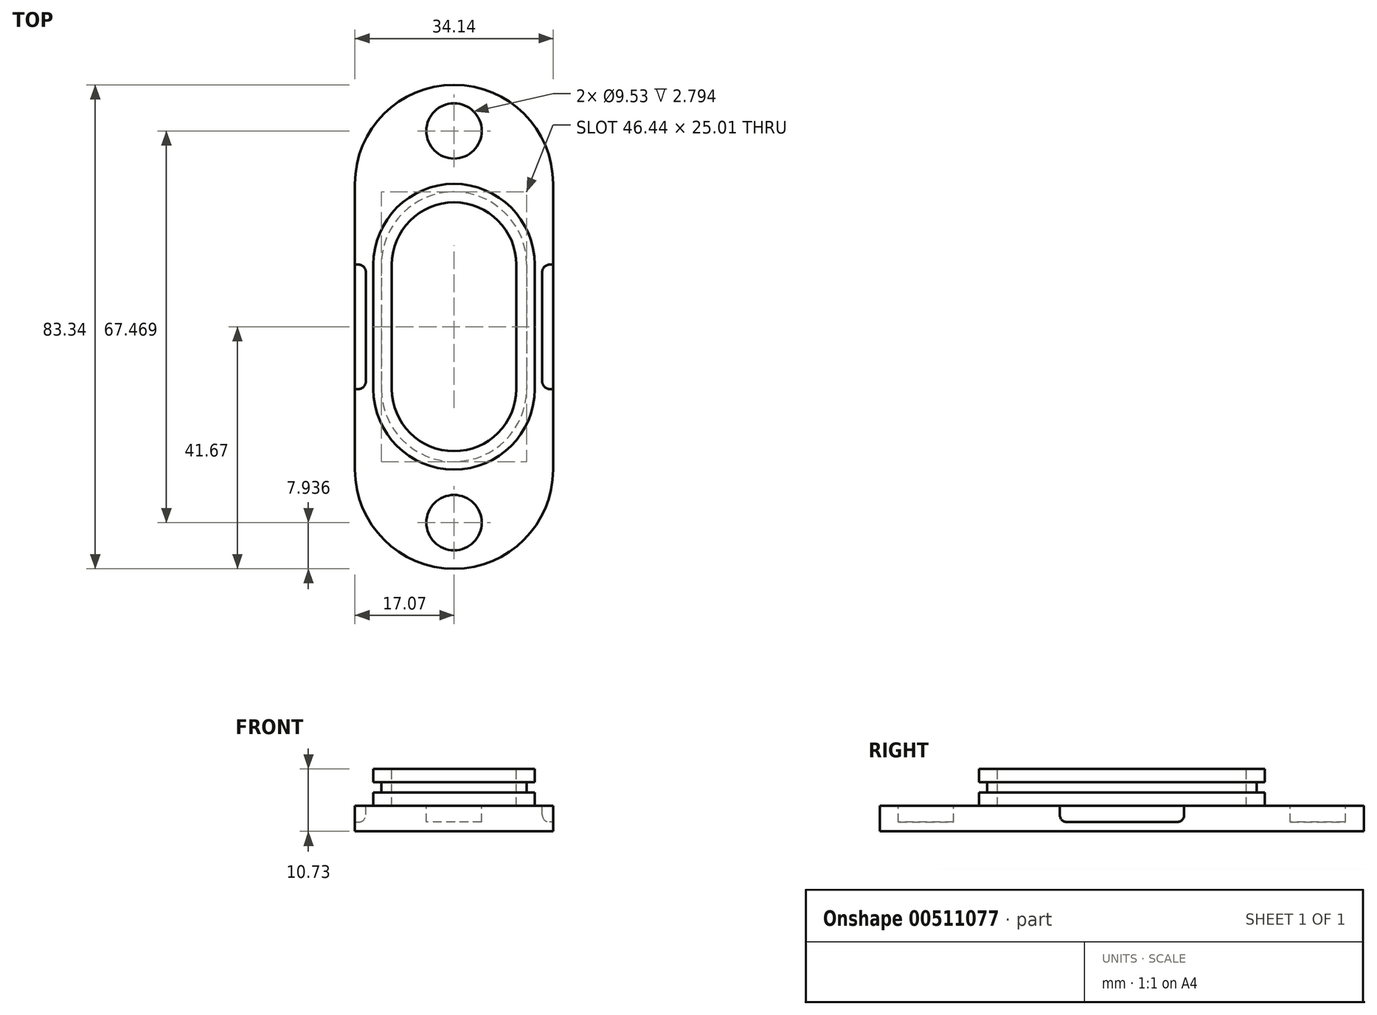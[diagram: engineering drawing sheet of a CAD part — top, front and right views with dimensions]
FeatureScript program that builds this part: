
annotation { "Feature Type Name" : "Feature", "Feature Type Description" : "" }
export const myFeature = defineFeature(function(context is Context, id is Id, definition is map)
    precondition{}
    {
        {
            var Q0;
            Q0=qCreatedBy(makeId("Top.planeOp"),FACE);
            var sketch = newSketch(context, id + "F0", { "sketchPlane" : qUnion([Q0])});
            skLineSegment(sketch, "E0.bottom", {"start": v(-13.9, 10.72) * mm, "end": v(13.9, 10.72) * mm, "construction": true});
            skLineSegment(sketch, "E0.top", {"start": v(-13.9, -10.72) * mm, "end": v(13.9, -10.72) * mm, "construction": true});
            skLineSegment(sketch, "E0.left", {"start": v(-13.9, 10.72) * mm, "end": v(-13.9, -10.72) * mm});
            skLineSegment(sketch, "E0.right", {"start": v(13.9, 10.72) * mm, "end": v(13.9, -10.72) * mm});
            skPoint(sketch, "E0.middle", {"position": v(0, 0) * mm});
            skArc(sketch, "E1", {"start": v(13.9, 10.72) * mm, "mid": v(0, 24.6) * mm, "end": v(-13.9, 10.72) * mm});
            skArc(sketch, "E2", {"start": v(-13.9, -10.72) * mm, "mid": v(0, -24.6) * mm, "end": v(13.9, -10.72) * mm});
            skLineSegment(sketch, "E3.bottom", {"start": v(-17.07, 24.6) * mm, "end": v(17.07, 24.6) * mm, "construction": true});
            skLineSegment(sketch, "E3.top", {"start": v(-17.07, -24.6) * mm, "end": v(17.07, -24.6) * mm, "construction": true});
            skLineSegment(sketch, "E3.left", {"start": v(-17.07, 24.6) * mm, "end": v(-17.07, -24.6) * mm});
            skLineSegment(sketch, "E3.right", {"start": v(17.07, 24.6) * mm, "end": v(17.07, -24.6) * mm});
            skArc(sketch, "E4", {"start": v(17.07, 24.6) * mm, "mid": v(0, 41.67) * mm, "end": v(-17.07, 24.6) * mm});
            skArc(sketch, "E5", {"start": v(-17.07, -24.6) * mm, "mid": v(0, -41.67) * mm, "end": v(17.07, -24.6) * mm});
            skCircle(sketch, "E6", {"center": v(0, 33.73) * mm, "radius": 4.76 * mm});
            skCircle(sketch, "E7", {"center": v(0, -33.73) * mm, "radius": 4.76 * mm});
            skArc(sketch, "E8.0", {"start": v(14.68, 10.72) * mm, "mid": v(0, 25.4) * mm, "end": v(-14.68, 10.72) * mm});
            skLineSegment(sketch, "E8.1", {"start": v(14.68, 10.72) * mm, "end": v(14.68, -10.72) * mm});
            skArc(sketch, "E8.2", {"start": v(-14.68, -10.72) * mm, "mid": v(0, -25.4) * mm, "end": v(14.68, -10.72) * mm});
            skLineSegment(sketch, "E8.3", {"start": v(-14.68, 10.72) * mm, "end": v(-14.68, -10.72) * mm});
            skSolve(sketch);
        }
        {
            var Q0;
            Q0=makeQuery(id+"F0.imprint","IMPRINT",FACE,{"disambiguationData":[TD([[makeQuery(id+"F0.imprint","IMPRINT",EDGE,{"derivedFrom":sQuery(id+"F0.wireOp",EDGE,"E0.left")}),1.0]])]});
            extrude(context, id + "F1", {"entities" : qUnion([Q0]), "depth" : 6.35 * mm});
        }
        {
            var Q0;
            Q0=makeQuery(id+"F0.imprint","IMPRINT",FACE,{"disambiguationData":[TD([[makeQuery(id+"F0.imprint","IMPRINT",EDGE,{"derivedFrom":sQuery(id+"F0.wireOp",EDGE,"E0.left")}),-1.0]])]});
            var Q1;
            Q1=makeQuery(id+"F0.imprint","IMPRINT",FACE,{"disambiguationData":[TD([[makeQuery(id+"F0.imprint","IMPRINT",EDGE,{"derivedFrom":sQuery(id+"F0.wireOp",EDGE,"E0.left")}),1.0]])]});
            var Q2;
            Q2=makeQuery(id+"F0.imprint","IMPRINT",FACE,{"disambiguationData":[TD([[makeQuery(id+"F0.imprint","IMPRINT",EDGE,{"derivedFrom":sQuery(id+"F0.wireOp",EDGE,"E3.left")}),1.0]])]});
            extrude(context, id + "F2", {"entities" : qUnion([Q0, Q1, Q2]), "operationType" : NewBodyOperationType.ADD, "oppositeDirection" : true, "depth" : 2.8 * mm});
        }
        {
            var Q0;
            Q0=makeQuery(id+"F2.opExtrude","CAP_FACE",FACE,{"disambiguationData":[OSD([sQuery(id+"F0.wireOp",EDGE,"E0.left"),sQuery(id+"F0.wireOp",EDGE,"E0.right"),sQuery(id+"F0.wireOp",EDGE,"E1"),sQuery(id+"F0.wireOp",EDGE,"E2"),sQuery(id+"F0.wireOp",EDGE,"E3.left"),sQuery(id+"F0.wireOp",EDGE,"E3.right"),sQuery(id+"F0.wireOp",EDGE,"E4"),sQuery(id+"F0.wireOp",EDGE,"E5"),sQuery(id+"F0.wireOp",EDGE,"E6"),sQuery(id+"F0.wireOp",EDGE,"E7")])],"isStart":false});
            var sketch = newSketch(context, id + "F3", { "sketchPlane" : qUnion([Q0])});
            skArc(sketch, "E9.0", {"start": v(-17.07, 24.6) * mm, "mid": v(0, 41.67) * mm, "end": v(17.07, 24.6) * mm});
            skLineSegment(sketch, "E10.0", {"start": v(17.07, -24.6) * mm, "end": v(17.07, 24.6) * mm});
            skArc(sketch, "E11.0", {"start": v(17.07, -24.6) * mm, "mid": v(0, -41.67) * mm, "end": v(-17.07, -24.6) * mm});
            skLineSegment(sketch, "E12.0", {"start": v(-17.07, -24.6) * mm, "end": v(-17.07, 24.6) * mm});
            skSolve(sketch);
        }
        {
            var Q0;
            Q0=qSketchRegion(id+"F3",true);
            extrude(context, id + "F4", {"entities" : qUnion([Q0]), "operationType" : NewBodyOperationType.ADD, "depth" : 1.59 * mm});
        }
        {
            var Q0;
            Q0=makeQuery(id+"F1.opExtrude","CAP_FACE",FACE,{"disambiguationData":[OSD([sQuery(id+"F0.wireOp",EDGE,"E0.left"),sQuery(id+"F0.wireOp",EDGE,"E0.right"),sQuery(id+"F0.wireOp",EDGE,"E1"),sQuery(id+"F0.wireOp",EDGE,"E2")])],"isStart":false});
            var sketch = newSketch(context, id + "F5", { "sketchPlane" : qUnion([Q0])});
            skLineSegment(sketch, "E13.0", {"start": v(-10.72, 10.72) * mm, "end": v(-10.72, -10.72) * mm});
            skArc(sketch, "E13.1", {"start": v(10.72, 10.72) * mm, "mid": v(0, 21.43) * mm, "end": v(-10.72, 10.72) * mm});
            skLineSegment(sketch, "E13.2", {"start": v(10.72, 10.72) * mm, "end": v(10.72, -10.72) * mm});
            skArc(sketch, "E13.3", {"start": v(-10.72, -10.72) * mm, "mid": v(0, -21.43) * mm, "end": v(10.72, -10.72) * mm});
            skSolve(sketch);
        }
        {
            var Q0;
            Q0=makeQuery(id+"F5.imprint","IMPRINT",FACE,{"disambiguationData":[TD([[makeQuery(id+"F5.imprint","IMPRINT",EDGE,{"derivedFrom":sQuery(id+"F5.wireOp",EDGE,"E13.0")}),1.0]])]});
            var Q1;
            Q1=makeQuery(id+"F2.opExtrude","CAP_FACE",FACE,{"disambiguationData":[OSD([sQuery(id+"F0.wireOp",EDGE,"E3.left"),sQuery(id+"F0.wireOp",EDGE,"E3.right"),sQuery(id+"F0.wireOp",EDGE,"E4"),sQuery(id+"F0.wireOp",EDGE,"E5"),sQuery(id+"F0.wireOp",EDGE,"E6"),sQuery(id+"F0.wireOp",EDGE,"E7")])],"isStart":true});
            extrude(context, id + "F6", {"entities" : qUnion([Q0]), "operationType" : NewBodyOperationType.REMOVE, "endBound" : BoundingType.UP_TO_SURFACE, "oppositeDirection" : true, "endBoundEntityFace" : qUnion([Q1]), "depth" : 6.35 * mm});
        }
        {
            var Q0;
            Q0=makeQuery(id+"F1.opExtrude","CAP_FACE",FACE,{"disambiguationData":[OSD([sQuery(id+"F0.wireOp",EDGE,"E0.left"),sQuery(id+"F0.wireOp",EDGE,"E0.right"),sQuery(id+"F0.wireOp",EDGE,"E1"),sQuery(id+"F0.wireOp",EDGE,"E2")])],"isStart":false});
            var Q1;
            Q1=makeQuery(id+"F0.imprint","IMPRINT",FACE,{"disambiguationData":[TD([[makeQuery(id+"F0.imprint","IMPRINT",EDGE,{"derivedFrom":sQuery(id+"F0.wireOp",EDGE,"E3.left")}),1.0]])]});
            cPlane(context, id + "F7", {"entities" : qUnion([Q0, Q1]), "cplaneType" : CPlaneType.MID_PLANE, "offset" : 25.4 * mm, "width" : 152.4 * mm, "height" : 152.4 * mm});
        }
        {
            var Q0;
            Q0=makeQuery(id+"F0.imprint","IMPRINT",FACE,{"disambiguationData":[TD([[makeQuery(id+"F0.imprint","IMPRINT",EDGE,{"derivedFrom":sQuery(id+"F0.wireOp",EDGE,"E3.left")}),1.0]])]});
            var sketch = newSketch(context, id + "F8", { "sketchPlane" : qUnion([Q0])});
            skLineSegment(sketch, "E14.bottom", {"start": v(-17.07, 10.72) * mm, "end": v(-15.2, 10.72) * mm});
            skLineSegment(sketch, "E14.top", {"start": v(-17.07, -10.72) * mm, "end": v(-15.2, -10.72) * mm});
            skLineSegment(sketch, "E14.left", {"start": v(-17.07, 10.72) * mm, "end": v(-17.07, -10.72) * mm});
            skLineSegment(sketch, "E14.right", {"start": v(-15.2, 10.72) * mm, "end": v(-15.2, -10.72) * mm});
            skLineSegment(sketch, "E15.bottom", {"start": v(17.07, 10.72) * mm, "end": v(15.2, 10.72) * mm});
            skLineSegment(sketch, "E15.top", {"start": v(17.07, -10.72) * mm, "end": v(15.2, -10.72) * mm});
            skLineSegment(sketch, "E15.left", {"start": v(17.07, 10.72) * mm, "end": v(17.07, -10.72) * mm});
            skLineSegment(sketch, "E15.right", {"start": v(15.2, 10.72) * mm, "end": v(15.2, -10.72) * mm});
            skSolve(sketch);
        }
        {
            var Q0;
            Q0=makeQuery(id+"F8.imprint","IMPRINT",FACE,{"disambiguationData":[TD([[makeQuery(id+"F8.imprint","IMPRINT",EDGE,{"derivedFrom":sQuery(id+"F8.wireOp",EDGE,"E15.bottom")}),1.0]])]});
            var Q1;
            Q1=makeQuery(id+"F8.imprint","IMPRINT",FACE,{"disambiguationData":[TD([[makeQuery(id+"F8.imprint","IMPRINT",EDGE,{"derivedFrom":sQuery(id+"F8.wireOp",EDGE,"E14.bottom")}),-1.0]])]});
            var Q2;
            Q2=makeQuery(id+"F4.boolean.opBoolean","SPLIT",FACE,{"disambiguationData":[TD([makeQuery(id+"F2.opExtrude","SWEPT_FACE",FACE,{"disambiguationData":[OSD([sQuery(id+"F0.wireOp",EDGE,"E7")])]})])],"derivedFrom":makeQuery(id+"F4.opExtrude","CAP_FACE",FACE,{"disambiguationData":[OSD([sQuery(id+"F3.wireOp",EDGE,"E9.0"),sQuery(id+"F3.wireOp",EDGE,"E10.0"),sQuery(id+"F3.wireOp",EDGE,"E11.0"),sQuery(id+"F3.wireOp",EDGE,"E12.0")])],"isStart":true})});
            extrude(context, id + "F9", {"entities" : qUnion([Q0, Q1]), "operationType" : NewBodyOperationType.REMOVE, "endBound" : BoundingType.UP_TO_SURFACE, "oppositeDirection" : true, "endBoundEntityFace" : qUnion([Q2]), "depth" : 25.4 * mm});
        }
        {
            var Q0;
            Q0=qCreatedBy(id+"F7.planeOp",FACE);
            var sketch = newSketch(context, id + "F10", { "sketchPlane" : qUnion([Q0])});
            skPoint(sketch, "E16.0", {"position": v(0, 25.4) * mm});
            skArc(sketch, "E17.0", {"start": v(14.68, 10.72) * mm, "mid": v(0, 25.4) * mm, "end": v(-14.68, 10.72) * mm});
            skLineSegment(sketch, "E18.0", {"start": v(14.68, 10.72) * mm, "end": v(14.68, -10.72) * mm});
            skLineSegment(sketch, "E19.0", {"start": v(-14.68, 10.72) * mm, "end": v(-14.68, -10.72) * mm});
            skArc(sketch, "E20.0", {"start": v(-14.68, -10.72) * mm, "mid": v(0, -25.4) * mm, "end": v(14.68, -10.72) * mm});
            skArc(sketch, "E21.0", {"start": v(12.5, 10.72) * mm, "mid": v(0, 23.22) * mm, "end": v(-12.5, 10.72) * mm});
            skLineSegment(sketch, "E21.1", {"start": v(12.5, 10.72) * mm, "end": v(12.5, -10.72) * mm});
            skArc(sketch, "E21.2", {"start": v(-12.5, -10.72) * mm, "mid": v(0, -23.22) * mm, "end": v(12.5, -10.72) * mm});
            skLineSegment(sketch, "E21.3", {"start": v(-12.5, 10.72) * mm, "end": v(-12.5, -10.72) * mm});
            skSolve(sketch);
        }
        {
            var Q0;
            Q0 = qSketchRegion(id + "F10", true);
            extrude(context, id + "F11", {"entities" : qUnion([Q0]), "operationType" : NewBodyOperationType.REMOVE, "endBound" : BoundingType.SYMMETRIC, "oppositeDirection" : true, "depth" : 1.78 * mm, "offsetDistance" : 25.4 * mm});
        }
        {
            var Q0;
            Q0=makeQuery(id+"F9.boolean.opBoolean","COPY",EDGE,{"derivedFrom":makeQuery(id+"F9.opExtrude","SWEPT_EDGE",EDGE,{"disambiguationData":[OSD([sQuery(id+"F8.wireOp",EDGE,"E15.top"),sQuery(id+"F8.wireOp",EDGE,"E15.right")])]})});
            var Q1;
            Q1=makeQuery(id+"F9.boolean.opBoolean","COPY",EDGE,{"derivedFrom":makeQuery(id+"F9.opExtrude","SWEPT_EDGE",EDGE,{"disambiguationData":[OSD([sQuery(id+"F8.wireOp",EDGE,"E15.bottom"),sQuery(id+"F8.wireOp",EDGE,"E15.right")])]})});
            var Q2;
            Q2=makeQuery(id+"F9.boolean.opBoolean","COPY",EDGE,{"derivedFrom":makeQuery(id+"F9.opExtrude","SWEPT_EDGE",EDGE,{"disambiguationData":[OSD([sQuery(id+"F8.wireOp",EDGE,"E14.bottom"),sQuery(id+"F8.wireOp",EDGE,"E14.right")])]})});
            var Q3;
            Q3=makeQuery(id+"F9.boolean.opBoolean","COPY",EDGE,{"derivedFrom":makeQuery(id+"F9.opExtrude","SWEPT_EDGE",EDGE,{"disambiguationData":[OSD([sQuery(id+"F8.wireOp",EDGE,"E14.top"),sQuery(id+"F8.wireOp",EDGE,"E14.right")])]})});
            fillet(context, id + "F12", {"entities" : qUnion([Q0, Q1, Q2, Q3]), "radius" : 1.27 * mm, "tangentPropagation" : true, "allowEdgeOverflow" : false});
        }
        {
            var Q0;
            Q0=makeQuery(id+"F9.boolean.opBoolean","COPY",EDGE,{"derivedFrom":makeQuery(id+"F9.opExtrude","CAP_EDGE",EDGE,{"disambiguationData":[OSD([sQuery(id+"F8.wireOp",EDGE,"E15.top")])],"isStart":true})});
            var Q1;
            Q1=makeQuery(id+"F9.boolean.opBoolean","COPY",EDGE,{"derivedFrom":makeQuery(id+"F9.opExtrude","CAP_EDGE",EDGE,{"disambiguationData":[OSD([sQuery(id+"F8.wireOp",EDGE,"E15.bottom")])],"isStart":true})});
            var Q2;
            Q2=makeQuery(id+"F9.boolean.opBoolean","COPY",EDGE,{"derivedFrom":makeQuery(id+"F9.opExtrude","CAP_EDGE",EDGE,{"disambiguationData":[OSD([sQuery(id+"F8.wireOp",EDGE,"E15.top")])],"isStart":false})});
            var Q3;
            Q3=makeQuery(id+"F9.boolean.opBoolean","COPY",EDGE,{"derivedFrom":makeQuery(id+"F9.opExtrude","CAP_EDGE",EDGE,{"disambiguationData":[OSD([sQuery(id+"F8.wireOp",EDGE,"E15.bottom")])],"isStart":false})});
            var Q4;
            Q4=makeQuery(id+"F9.boolean.opBoolean","COPY",EDGE,{"derivedFrom":makeQuery(id+"F9.opExtrude","CAP_EDGE",EDGE,{"disambiguationData":[OSD([sQuery(id+"F8.wireOp",EDGE,"E14.top")])],"isStart":true})});
            var Q5;
            Q5=makeQuery(id+"F9.boolean.opBoolean","COPY",EDGE,{"derivedFrom":makeQuery(id+"F9.opExtrude","CAP_EDGE",EDGE,{"disambiguationData":[OSD([sQuery(id+"F8.wireOp",EDGE,"E14.top")])],"isStart":false})});
            var Q6;
            Q6=makeQuery(id+"F9.boolean.opBoolean","COPY",EDGE,{"derivedFrom":makeQuery(id+"F9.opExtrude","CAP_EDGE",EDGE,{"disambiguationData":[OSD([sQuery(id+"F8.wireOp",EDGE,"E14.bottom")])],"isStart":true})});
            var Q7;
            Q7=makeQuery(id+"F9.boolean.opBoolean","COPY",EDGE,{"derivedFrom":makeQuery(id+"F9.opExtrude","CAP_EDGE",EDGE,{"disambiguationData":[OSD([sQuery(id+"F8.wireOp",EDGE,"E14.bottom")])],"isStart":false})});
            fillet(context, id + "F13", {"entities" : qUnion([Q0, Q1, Q2, Q3, Q4, Q5, Q6, Q7]), "radius" : 1.27 * mm, "tangentPropagation" : true, "allowEdgeOverflow" : false});
        }
    });
